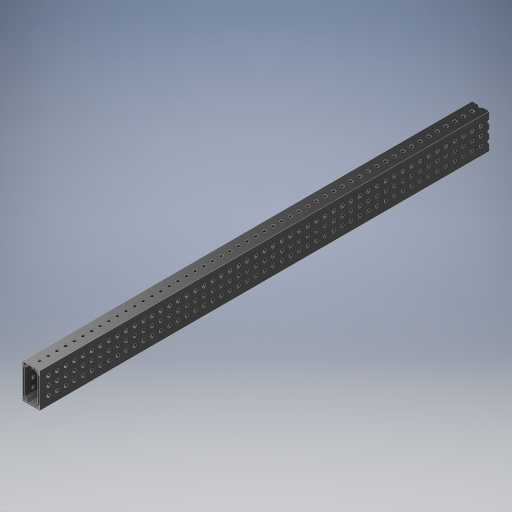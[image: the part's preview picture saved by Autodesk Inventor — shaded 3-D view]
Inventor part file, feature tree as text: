
AUTODESK INVENTOR PART (.ipt)
format: ipt  version: 2024.2 (Build 282272000, 272)  size: 1,197,568 bytes
history: native  units: in
note: dims shown in document units (in); Inventor stores cm internally (conversion verified against a paired STEP export)
features: other x13, extrude x9, hole x3, pattern_linear x3, mirror x3, sheet_metal_op x1, plane x1
ambient origin geometry x8: Origin, YZ Plane, XZ Plane, XY Plane, X Axis, Y Axis, Z Axis, Center Point
bodies: Solid1 (feature_tree)
feature tree (33):
  other  "MAXTube"
  other  "Blocks"
  other  "Base Sketch"
  extrude  "Base"  Depth=2.0in
  extrude  "MAX Corner"  Depth=1.0in
  extrude  "MAX Corner Cut"  Depth=0.125in
  extrude  "Scribe Lines"  Depth=0.04in
  other  "Side Middle"
  other  "Top Middle"
  other  "Side Holes Sketch"
  hole  "Top Side Hole"  [1 undecoded]
  hole  "Mid Side Hole"  [1 undecoded]
  hole  "Btm Side Hole"  [1 undecoded]
  pattern_linear  "Side Holes"  Spacing1=0.04in  [1 undecoded]
  mirror  "Side Mirror"
  extrude  "MAXTube Hole"  Depth=0.04in
  extrude  "MAXTube Outside"  Depth=26.0in
  pattern_linear  "MAXTube Pattern"  Spacing1=0.0in  [1 undecoded]
  mirror  "MAXTube Mirror"
  extrude  "Left Top Hole"  Depth=26.0in
  extrude  "Mid Top Hole"  TaperAngle=0.0deg  [1 undecoded]
  extrude  "Right Top Hole"  TaperAngle=0.0deg  [1 undecoded]
  pattern_linear  "Top Holes"  Spacing1=0.005in  [1 undecoded]
  mirror  "Top Mirror"
  sheet_metal_op  "Corner"
  plane  "Work Plane3"
  other  "Corner:5"
  other  "Corner:6"
  other  "Corner:7"
  other  "Corner:8"
  other  "MAXTube:1"
  other  "MAXTube:2"
  other  "MAXTube:3"
note: 8 required parameter values undecoded (feature->parameter linkage not recoverable at this tier; creation-order binding heuristic only, values carry confidence <= 0.55)
